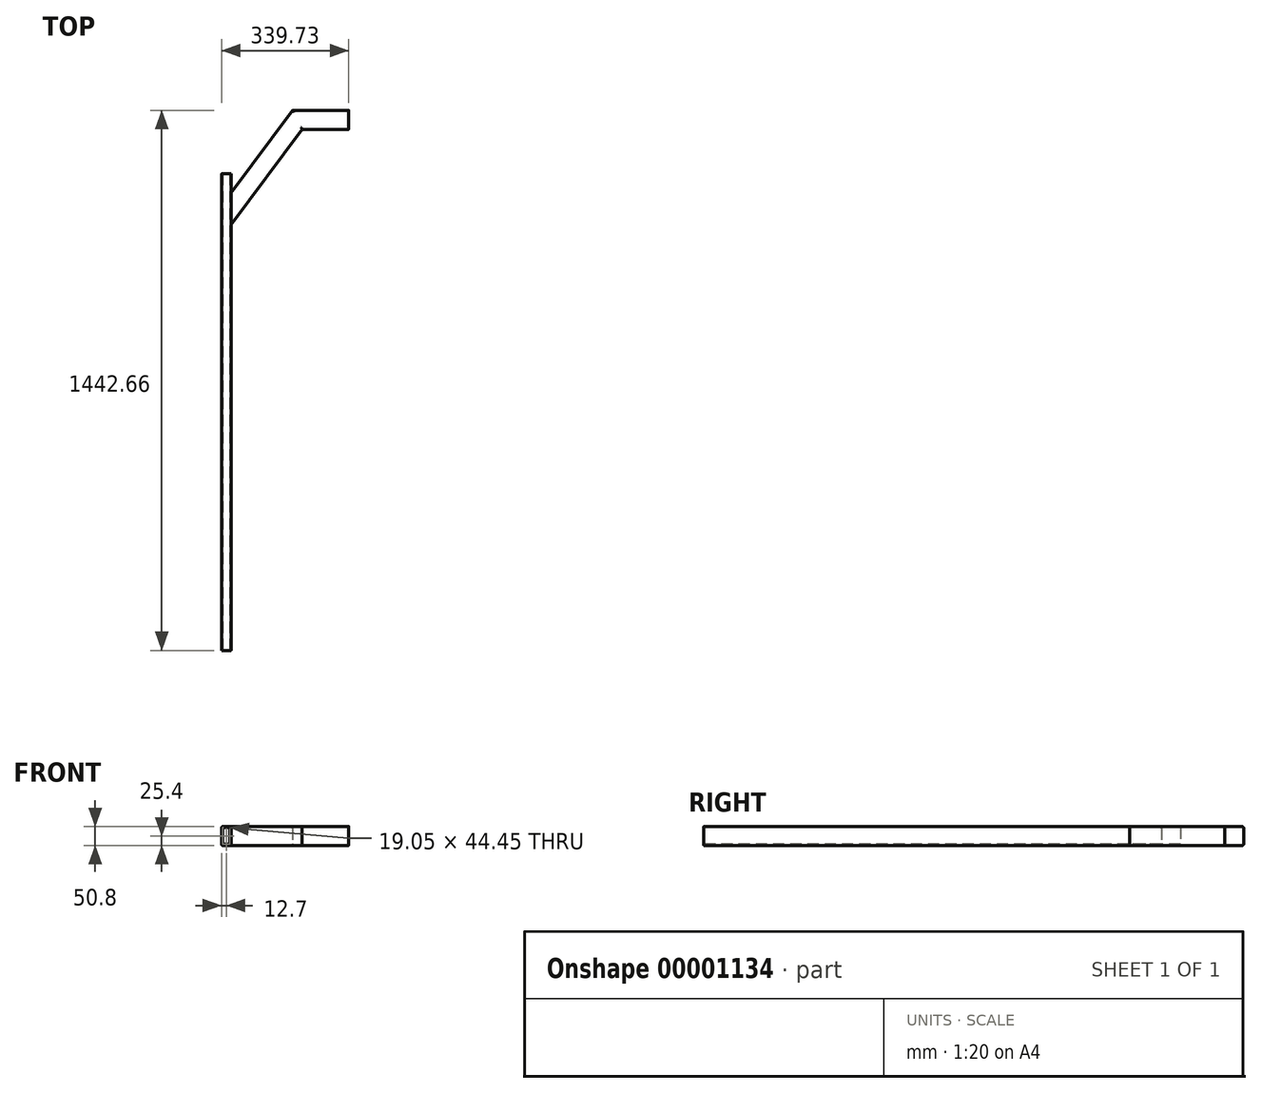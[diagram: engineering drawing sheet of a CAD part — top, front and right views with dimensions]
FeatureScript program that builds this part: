
annotation { "Feature Type Name" : "Feature", "Feature Type Description" : "" }
export const myFeature = defineFeature(function(context is Context, id is Id, definition is map)
    precondition{}
    {
        {
            var Q0;
            Q0=qCreatedBy(makeId("Top.planeOp"),FACE);
            var sketch = newSketch(context, id + "F0", { "sketchPlane" : qUnion([Q0])});
            skLineSegment(sketch, "E0.bottom", {"start": v(-25.4, 1024.15) * mm, "end": v(0, 1024.15) * mm});
            skLineSegment(sketch, "E0.top", {"start": v(-25.4, -249.02) * mm, "end": v(0, -249.02) * mm});
            skLineSegment(sketch, "E0.left", {"start": v(-25.4, 1024.15) * mm, "end": v(-25.4, -249.02) * mm});
            skLineSegment(sketch, "E0.right", {"start": v(0, 1024.15) * mm, "end": v(0, -249.02) * mm});
            skLineSegment(sketch, "E1", {"start": v(0, 973.35) * mm, "end": v(164.53, 1193.64) * mm});
            skLineSegment(sketch, "E2", {"start": v(164.53, 1193.64) * mm, "end": v(314.32, 1193.64) * mm});
            skLineSegment(sketch, "E3", {"start": v(314.32, 1193.64) * mm, "end": v(314.32, 1142.84) * mm});
            skLineSegment(sketch, "E4", {"start": v(314.32, 1142.84) * mm, "end": v(190, 1142.84) * mm});
            skLineSegment(sketch, "E5", {"start": v(190, 1142.84) * mm, "end": v(0, 888.46) * mm});
            skLineSegment(sketch, "E6.bottom", {"start": v(-25.4, 827.28) * mm, "end": v(-228.6, 827.28) * mm});
            skLineSegment(sketch, "E6.top", {"start": v(-25.4, 789.18) * mm, "end": v(-228.6, 789.18) * mm});
            skLineSegment(sketch, "E6.left", {"start": v(-25.4, 827.28) * mm, "end": v(-25.4, 789.18) * mm});
            skLineSegment(sketch, "E6.right", {"start": v(-228.6, 827.28) * mm, "end": v(-228.6, 789.18) * mm});
            skLineSegment(sketch, "E7.bottom", {"start": v(-25.4, 560.8) * mm, "end": v(-228.6, 560.8) * mm});
            skLineSegment(sketch, "E7.top", {"start": v(-25.4, 522.7) * mm, "end": v(-228.6, 522.7) * mm});
            skLineSegment(sketch, "E7.left", {"start": v(-25.4, 560.8) * mm, "end": v(-25.4, 522.7) * mm});
            skLineSegment(sketch, "E7.right", {"start": v(-228.6, 560.8) * mm, "end": v(-228.6, 522.7) * mm});
            skLineSegment(sketch, "E8.bottom", {"start": v(-25.4, 162.55) * mm, "end": v(-228.6, 162.55) * mm});
            skLineSegment(sketch, "E8.top", {"start": v(-25.4, 124.45) * mm, "end": v(-228.6, 124.45) * mm});
            skLineSegment(sketch, "E8.left", {"start": v(-25.4, 162.55) * mm, "end": v(-25.4, 124.45) * mm});
            skLineSegment(sketch, "E8.right", {"start": v(-228.6, 162.55) * mm, "end": v(-228.6, 124.45) * mm});
            skLineSegment(sketch, "E9.bottom", {"start": v(-101.6, 221.91) * mm, "end": v(-152.4, 221.91) * mm});
            skLineSegment(sketch, "E9.top", {"start": v(-101.6, 65.09) * mm, "end": v(-152.4, 65.09) * mm});
            skLineSegment(sketch, "E9.left", {"start": v(-101.6, 221.91) * mm, "end": v(-101.6, 65.09) * mm});
            skLineSegment(sketch, "E9.right", {"start": v(-152.4, 221.91) * mm, "end": v(-152.4, 65.09) * mm});
            skPoint(sketch, "E10", {"position": v(-127, 65.09) * mm});
            skPoint(sketch, "E11", {"position": v(-228.6, 143.5) * mm});
            skPoint(sketch, "E12", {"position": v(-152.4, 143.5) * mm});
            skPoint(sketch, "E13", {"position": v(-127, 124.45) * mm});
            skLineSegment(sketch, "E14", {"start": v(0, -149.42) * mm, "end": v(114.82, -502.8) * mm, "construction": true});
            skSolve(sketch);
        }
        {
            var Q0;
            {var subQ4=sQuery(id+"F0.wireOp",EDGE,"E0.bottom");Q0=makeQuery(id+"F0.imprint","IMPRINT",FACE,{"disambiguationData":[TD([[makeQuery(id+"F0.imprint","IMPRINT",EDGE,{"derivedFrom":subQ4}),-1.0]])]});}
            extrude(context, id + "F1", {"entities" : qUnion([Q0]), "depth" : 50.8 * mm});
        }
        {
            var Q0;
            Q0=makeQuery(id+"F1.opExtrude","SWEPT_FACE",FACE,{"disambiguationData":[OSD([sQuery(id+"F0.wireOp",EDGE,"E0.top")])]});
            var Q1;
            Q1=makeQuery(id+"F1.opExtrude","SWEPT_FACE",FACE,{"disambiguationData":[OSD([sQuery(id+"F0.wireOp",EDGE,"E0.bottom")])]});
            shell(context, id + "F2", {"entities" : qUnion([Q0, Q1]), "thickness" : 3.17 * mm});
        }
        {
            var Q0;
            Q0=makeQuery(id+"F1.opExtrude","CAP_EDGE",EDGE,{"disambiguationData":[OSD([sQuery(id+"F0.wireOp",EDGE,"E0.left"),sQuery(id+"F0.wireOp",EDGE,"E6.left"),sQuery(id+"F0.wireOp",EDGE,"E7.left"),sQuery(id+"F0.wireOp",EDGE,"E8.left")])],"isStart":false});
            var Q1;
            Q1=makeQuery(id+"F1.opExtrude","CAP_EDGE",EDGE,{"disambiguationData":[OSD([sQuery(id+"F0.wireOp",EDGE,"E0.left"),sQuery(id+"F0.wireOp",EDGE,"E6.left"),sQuery(id+"F0.wireOp",EDGE,"E7.left"),sQuery(id+"F0.wireOp",EDGE,"E8.left")])],"isStart":true});
            var Q2;
            Q2=makeQuery(id+"F1.opExtrude","CAP_EDGE",EDGE,{"disambiguationData":[OSD([sQuery(id+"F0.wireOp",EDGE,"E0.right")])],"isStart":true});
            var Q3;
            Q3=makeQuery(id+"F1.opExtrude","CAP_EDGE",EDGE,{"disambiguationData":[OSD([sQuery(id+"F0.wireOp",EDGE,"E0.right")])],"isStart":false});
            fillet(context, id + "F3", {"entities" : qUnion([Q0, Q1, Q2, Q3]), "radius" : 3.17 * mm, "tangentPropagation" : true, "allowEdgeOverflow" : false});
        }
        {
            var Q0;
            {var subQ0=sQuery(id+"F0.wireOp",EDGE,"E1");Q0=makeQuery(id+"F0.imprint","IMPRINT",FACE,{"disambiguationData":[TD([[makeQuery(id+"F0.imprint","IMPRINT",EDGE,{"derivedFrom":subQ0}),-1.0]])]});}
            extrude(context, id + "F4", {"entities" : qUnion([Q0]), "operationType" : NewBodyOperationType.ADD, "depth" : 50.8 * mm});
        }
        {
            var Q0;
            Q0=makeQuery(id+"F4.opExtrude","CAP_EDGE",EDGE,{"disambiguationData":[OSD([sQuery(id+"F0.wireOp",EDGE,"E1")])],"isStart":false});
            var Q1;
            Q1=makeQuery(id+"F4.opExtrude","CAP_EDGE",EDGE,{"disambiguationData":[OSD([sQuery(id+"F0.wireOp",EDGE,"E2")])],"isStart":false});
            var Q2;
            Q2=makeQuery(id+"F4.opExtrude","CAP_EDGE",EDGE,{"disambiguationData":[OSD([sQuery(id+"F0.wireOp",EDGE,"E1")])],"isStart":true});
            var Q3;
            Q3=makeQuery(id+"F4.opExtrude","CAP_EDGE",EDGE,{"disambiguationData":[OSD([sQuery(id+"F0.wireOp",EDGE,"E2")])],"isStart":true});
            var Q4;
            Q4=makeQuery(id+"F4.opExtrude","CAP_EDGE",EDGE,{"disambiguationData":[OSD([sQuery(id+"F0.wireOp",EDGE,"E5")])],"isStart":false});
            var Q5;
            Q5=makeQuery(id+"F4.opExtrude","CAP_EDGE",EDGE,{"disambiguationData":[OSD([sQuery(id+"F0.wireOp",EDGE,"E4")])],"isStart":false});
            var Q6;
            Q6=makeQuery(id+"F4.opExtrude","CAP_EDGE",EDGE,{"disambiguationData":[OSD([sQuery(id+"F0.wireOp",EDGE,"E5")])],"isStart":true});
            var Q7;
            Q7=makeQuery(id+"F4.opExtrude","CAP_EDGE",EDGE,{"disambiguationData":[OSD([sQuery(id+"F0.wireOp",EDGE,"E4")])],"isStart":true});
            fillet(context, id + "F5", {"entities" : qUnion([Q0, Q1, Q2, Q3, Q4, Q5, Q6, Q7]), "radius" : 5.08 * mm, "tangentPropagation" : true, "allowEdgeOverflow" : false});
        }
    });
